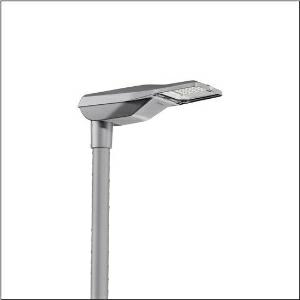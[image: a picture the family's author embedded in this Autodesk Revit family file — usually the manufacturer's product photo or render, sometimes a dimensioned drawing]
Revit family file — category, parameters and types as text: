
# Revit family: streetlight_sl_21_iq_micro___p0_8ab_5xe1r31d08db_6a63
name_source: partatom
category: Lighting Fixtures
units: mm (PartAtom-declared; Revit-internal decimal feet)

## family parameters
Cut with Voids When Loaded = No
Host = Face
Light Source = No
Part Type = Normal
Room Calculation Point = No
Round Connector Dimension = Use Diameter
Shared = No

## types (1)
- --- (1 x LED, 4220 lm, 36.4 W, 3000K)
    Apparent Load = 36 VA
    CIE Flux Codes = 36 71 98 100 100
    Color Rendering = 70
    Color Temperature = 3000K
    Default Elevation = 1800 mm
    Description = Streetlight SL 21 iQ micro, mast luminaire, primary light control with lens, of PMMA, primary optical cover: cover, of toughened safety glass, transparent, light distribution: P0.8aB, light emission: direct distribution, primary light characteristic: asymmetric, installation type: post-top, side-entry, LED, High Power LED, rated luminous flux: 4.220lm, luminous efficacy: 116lm/W, light colour: 730, colour temperature: 3000K, control gear: iQ-Comfort, control: pre-setting: linear dimming characteristic, Auto-Match, Temp-Guard, Lumen-Switch, Night-Set, Smart-Wire, Light-Fading, Desk-Remote (wireless, voltage-free reading and setting of iQ features in the workshop via application-optimized NFC function/RFID function), optimised constant luminous flux control (CLO 2.0), mains connection: 220..240V, AC, 50/60Hz, start of lifetime: 36W, end of service life: 38W, reduction: 16W, luminaire housing, of diecast aluminium, powder-coated, Siteco® metallic grey (DB 702S), corrosivity category C5 mid according to DIN EN ISO 12944, please order mast flange separately, inclination adjustable: 0°, 5°, 10°, 15°, sealing non-destructively replaceable, multi-level sealing system, length: 528mm, width: 235mm, height: 110mm, mast flange for spigot size: 42mm (side-entry): 5XC10008XM4, 60/48mm (side-entry/post-top): 5XC10108XM2, 76/60mm (side-entry/post-top): 5XC10108XM1, protection rating (complete): IP66, insulation class (complete): insulation class II (safety insulation), certification: CE, ENEC, ENEC+, VDE, impact resistance: IK09, permissible operating ambient temperature for outdoor applications: -40..+50°C, standard-compliant lighting for roads and squares, packaging unit: 1 piece

Light Distribution: P0.8aB
    Height = 110 mm
    Lamp = 1 x LED
    Lamp Light Flux = 4220 lm
    Lamp Power = 36.4 W
    Lamp count = 1
    Length = 528 mm
    Luminous efficacy = 116 lm/W
    Manufacturer = Siteco
    ModVariant = No
    Model = 5XE1R31D08DB
    Number of Poles = 1
    OnlyDefault = Yes
    Power Factor = 1
    Product Name = Streetlight SL 21 iQ micro | P0.8aB
    Product group = mast luminaire | pylon top
    ProductGroupID = 6100
    Protection Class = Protection class II
    Protection Degree = IP 66
    RLX_Detail_Level = 1
    RLX_Emergency_Light_Flux = 0 lm
    RLX_Emergency_Type = 0
    RLX_Emergency_Type_DB = No
    RlxData = <blob elided: 98393 chars, md5=6f9df660>
    Socket = socket
    Standby Power = 0 W
    System Light Flux = 4220 lm
    System Power = 36 W
    Type Comments = factory setting: luminous flux: 100 % | dim-lin: 254 | 715 mA
    Type Image = l_1006881.jpg
    URL = http://relux.com
    VarID = @adj_071866
    Voltage = 0 V
    Weight = 0.00 kg
    Width = 235 mm

## geometry (parser evidence)
native form markers: Blend x4, Sweep x12
no freeform markers — native parametric forms only
